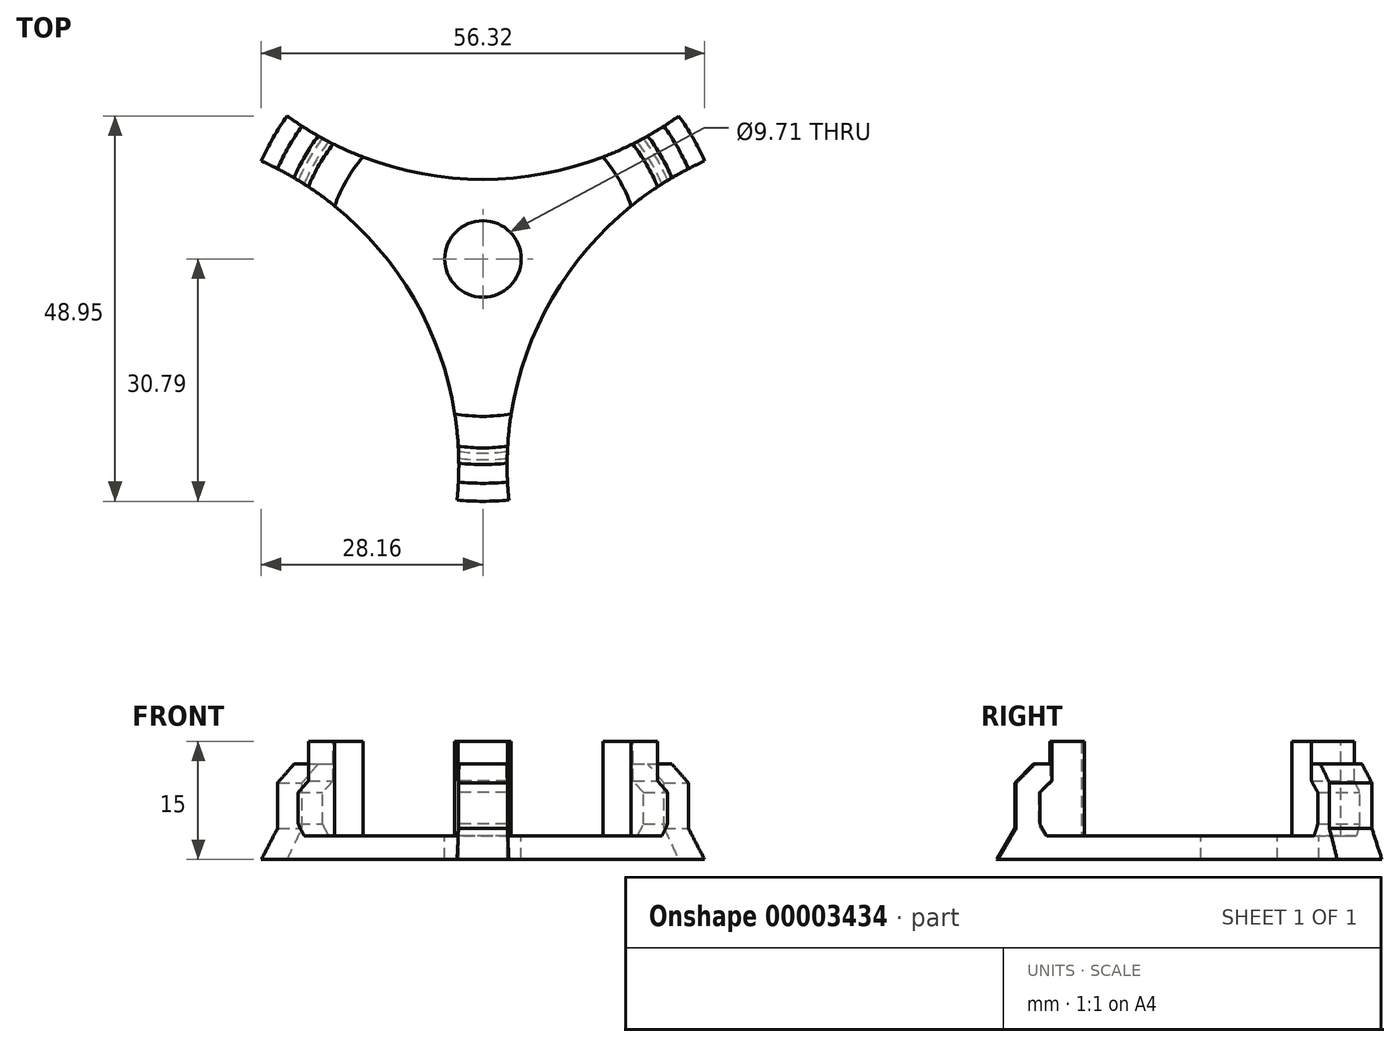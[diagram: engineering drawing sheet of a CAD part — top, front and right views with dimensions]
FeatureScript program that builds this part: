
annotation { "Feature Type Name" : "Feature", "Feature Type Description" : "" }
export const myFeature = defineFeature(function(context is Context, id is Id, definition is map)
    precondition{}
    {
        {
            var Q0;
            Q0=qCreatedBy(makeId("Front.planeOp"),FACE);
            var sketch = newSketch(context, id + "F0", { "sketchPlane" : qUnion([Q0])});
            skLineSegment(sketch, "E0", {"start": v(-20, 0) * mm, "end": v(-20, -12) * mm});
            skLineSegment(sketch, "E1", {"start": v(-20, -12) * mm, "end": v(-24.63, -12) * mm});
            skLineSegment(sketch, "E2", {"start": v(-24, 0) * mm, "end": v(-20, 0) * mm});
            skLineSegment(sketch, "E3", {"start": v(-24, 0) * mm, "end": v(-24, -5) * mm});
            skLineSegment(sketch, "E4", {"start": v(-24, -5) * mm, "end": v(-25.5, -6.5) * mm});
            skLineSegment(sketch, "E5", {"start": v(-25.5, -6.5) * mm, "end": v(-25.5, -10.5) * mm});
            skLineSegment(sketch, "E6", {"start": v(-25.5, -10.5) * mm, "end": v(-24.63, -12) * mm});
            skLineSegment(sketch, "E7", {"start": v(0, 0) * mm, "end": v(0, 22.88) * mm, "construction": true});
            skLineSegment(sketch, "E8", {"start": v(0, -12) * mm, "end": v(-24.63, -12) * mm});
            skLineSegment(sketch, "E9", {"start": v(-25.5, -10.5) * mm, "end": v(-25.5, -6.5) * mm});
            skLineSegment(sketch, "E10", {"start": v(-24, -5) * mm, "end": v(-24, -2.88) * mm});
            skLineSegment(sketch, "E11.0", {"start": v(-26.12, -2.88) * mm, "end": v(-28.5, -5.26) * mm});
            skLineSegment(sketch, "E11.1", {"start": v(-28.5, -5.26) * mm, "end": v(-28.5, -11.04) * mm});
            skLineSegment(sketch, "E11.3", {"start": v(0, -15) * mm, "end": v(-25.79, -15) * mm});
            skLineSegment(sketch, "E12", {"start": v(0, -12) * mm, "end": v(0, -15) * mm});
            skLineSegment(sketch, "E13", {"start": v(-26.12, -2.88) * mm, "end": v(-24, -2.88) * mm});
            skLineSegment(sketch, "E14", {"start": v(-25.79, -15) * mm, "end": v(-30.79, -15) * mm});
            skLineSegment(sketch, "E15", {"start": v(-30.79, -15) * mm, "end": v(-28.5, -11.04) * mm});
            skSolve(sketch);
        }
        {
            var Q0;
            Q0=makeQuery(id+"F0.imprint","IMPRINT",FACE,{"disambiguationData":[TD([[makeQuery(id+"F0.imprint","IMPRINT",EDGE,{"derivedFrom":sQuery(id+"F0.wireOp",EDGE,"E0")}),-1.0]])]});
            var Q1;
            Q1=sQuery(id+"F0.wireOp",EDGE,"E7");
            revolve(context, id + "F1", {"entities" : qUnion([Q0]), "axis" : qUnion([Q1]), "revolveType" : RevolveType.FULL});
        }
        {
            var Q0;
            Q0=qCreatedBy(makeId("Front.planeOp"),FACE);
            var sketch = newSketch(context, id + "F2", { "sketchPlane" : qUnion([Q0])});
            skLineSegment(sketch, "E16", {"start": v(0, 0) * mm, "end": v(0, 72.88) * mm, "construction": true});
            skSolve(sketch);
        }
        {
            var Q0;
            Q0=makeQuery(id+"F0.imprint","IMPRINT",FACE,{"disambiguationData":[TD([[makeQuery(id+"F0.imprint","IMPRINT",EDGE,{"derivedFrom":sQuery(id+"F0.wireOp",EDGE,"E4")}),-1.0]])]});
            var Q1;
            Q1=sQuery(id+"F2.wireOp",EDGE,"E16");
            revolve(context, id + "F3", {"entities" : qUnion([Q0]), "axis" : qUnion([Q1]), "revolveType" : RevolveType.FULL});
        }
        {
            var Q0;
            Q0=qCreatedBy(makeId("Top.planeOp"),FACE);
            var sketch = newSketch(context, id + "F4", { "sketchPlane" : qUnion([Q0])});
            skArc(sketch, "E17", {"start": v(-24.87, 18.16) * mm, "mid": v(0, 10.11) * mm, "end": v(24.87, 18.16) * mm});
            skArc(sketch, "E18.1.0", {"start": v(-3.3, -30.61) * mm, "mid": v(-8.76, -5.06) * mm, "end": v(-28.16, 12.46) * mm});
            skArc(sketch, "E18.2.0", {"start": v(28.16, 12.46) * mm, "mid": v(8.76, -5.06) * mm, "end": v(3.3, -30.61) * mm});
            skPoint(sketch, "E18.center", {"position": v(0, 0) * mm});
            skCircle(sketch, "E19", {"center": v(0, 0) * mm, "radius": 30.79 * mm});
            skCircle(sketch, "E20", {"center": v(0, 0) * mm, "radius": 4.85 * mm});
            skSolve(sketch);
        }
        {
            var Q0;
            {var subQ1=sQuery(id+"F4.wireOp",EDGE,"E17");Q0=makeQuery(id+"F4.imprint","IMPRINT",FACE,{"disambiguationData":[TD([[makeQuery(id+"F4.imprint","IMPRINT",EDGE,{"derivedFrom":subQ1}),1.0]])]});}
            var Q1;
            {var subQ1=sQuery(id+"F4.wireOp",EDGE,"E18.2.0");Q1=makeQuery(id+"F4.imprint","IMPRINT",FACE,{"disambiguationData":[TD([[makeQuery(id+"F4.imprint","IMPRINT",EDGE,{"derivedFrom":subQ1}),1.0]])]});}
            var Q2;
            {var subQ1=sQuery(id+"F4.wireOp",EDGE,"E18.1.0");Q2=makeQuery(id+"F4.imprint","IMPRINT",FACE,{"disambiguationData":[TD([[makeQuery(id+"F4.imprint","IMPRINT",EDGE,{"derivedFrom":subQ1}),1.0]])]});}
            var Q3;
            Q3=makeQuery(id+"F4.imprint","IMPRINT",FACE,{"disambiguationData":[TD([[makeQuery(id+"F4.imprint","IMPRINT",EDGE,{"derivedFrom":sQuery(id+"F4.wireOp",EDGE,"E20")}),1.0]])]});
            extrude(context, id + "F5", {"entities" : qUnion([Q0, Q1, Q2, Q3]), "operationType" : NewBodyOperationType.REMOVE, "endBound" : BoundingType.THROUGH_ALL, "oppositeDirection" : true, "depth" : 25 * mm});
        }
    });
